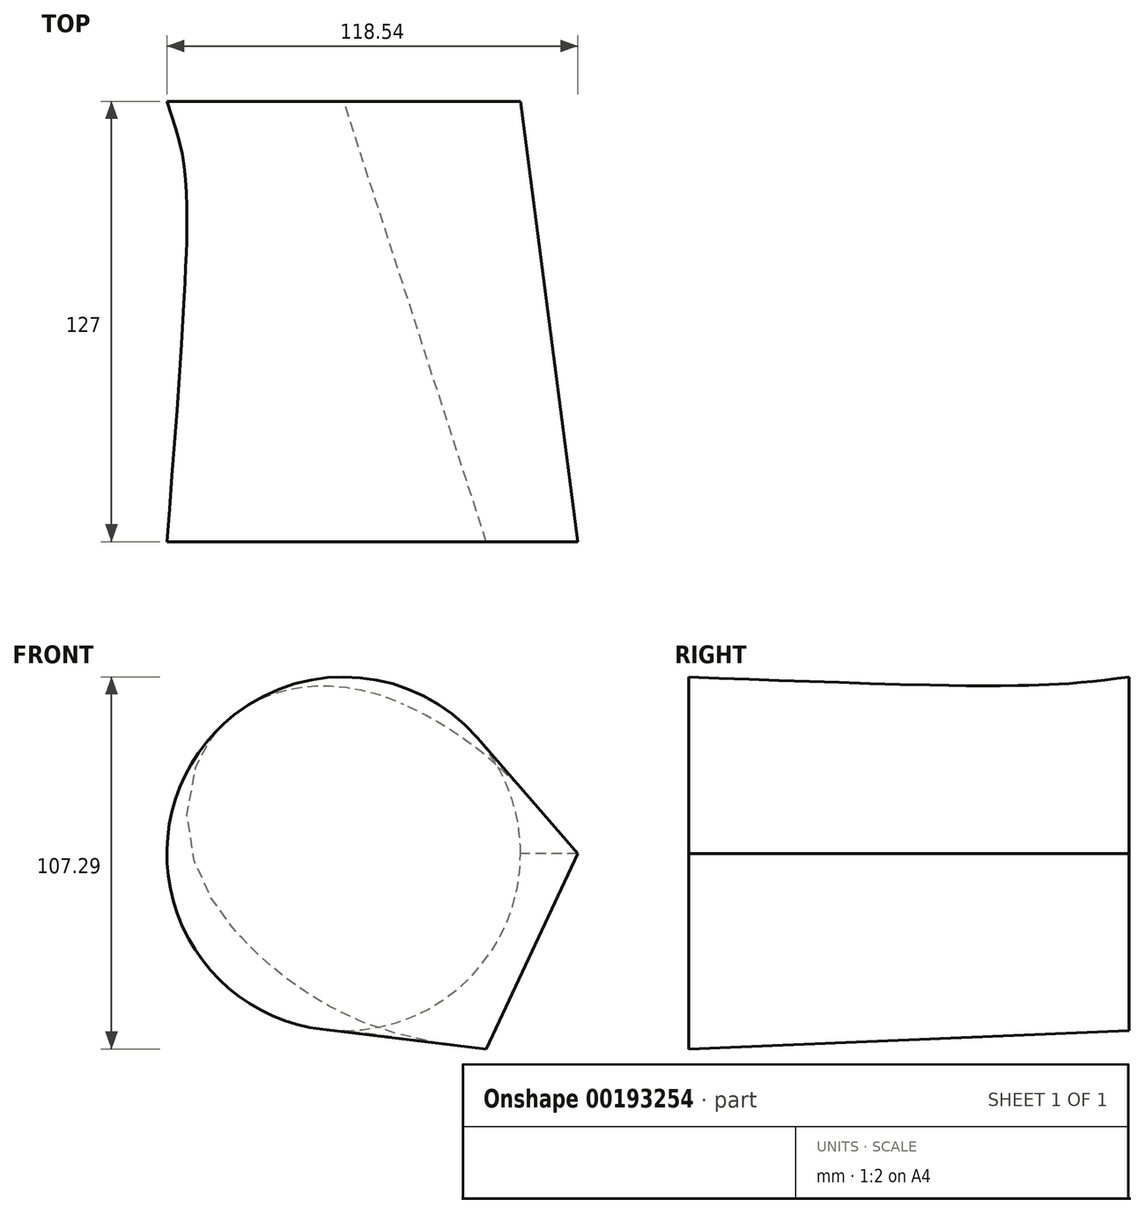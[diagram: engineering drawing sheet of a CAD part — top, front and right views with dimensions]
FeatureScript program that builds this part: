
annotation { "Feature Type Name" : "Feature", "Feature Type Description" : "" }
export const myFeature = defineFeature(function(context is Context, id is Id, definition is map)
    precondition{}
    {
        {
            var Q0;
            Q0=qCreatedBy(makeId("Front.planeOp"),FACE);
            cPlane(context, id + "F0", {"entities" : qUnion([Q0]), "cplaneType" : CPlaneType.OFFSET, "offset" : 127 * mm, "width" : 152.4 * mm, "height" : 152.4 * mm});
        }
        {
            var Q0;
            Q0=qCreatedBy(makeId("Front.planeOp"),FACE);
            var sketch = newSketch(context, id + "F1", { "sketchPlane" : qUnion([Q0])});
            skCircle(sketch, "E0", {"center": v(0, 0) * mm, "radius": 51 * mm});
            skPoint(sketch, "E1", {"position": v(51, 0) * mm});
            skSolve(sketch);
        }
        {
            var Q0;
            Q0=qCreatedBy(id+"F0.planeOp",FACE);
            var sketch = newSketch(context, id + "F2", { "sketchPlane" : qUnion([Q0])});
            skArc(sketch, "E2.0", {"start": v(38.53, 33.43) * mm, "mid": v(-45.07, 23.9) * mm, "end": v(-6.04, -50.65) * mm});
            skLineSegment(sketch, "E3", {"start": v(38.53, 33.43) * mm, "end": v(67.53, 0) * mm});
            skLineSegment(sketch, "E4", {"start": v(67.53, 0) * mm, "end": v(41.12, -56.28) * mm});
            skLineSegment(sketch, "E5", {"start": v(41.12, -56.28) * mm, "end": v(-6.04, -50.65) * mm});
            skSolve(sketch);
        }
        {
            var Q0;
            Q0=makeQuery(id+"F2.imprint","IMPRINT",FACE,{"disambiguationData":[TD([[makeQuery(id+"F2.imprint","IMPRINT",EDGE,{"derivedFrom":sQuery(id+"F2.wireOp",EDGE,"E2.0")}),1.0]])]});
            var Q1;
            Q1=makeQuery(id+"F1.imprint","IMPRINT",FACE,{"disambiguationData":[TD([[makeQuery(id+"F1.imprint","IMPRINT",EDGE,{"derivedFrom":sQuery(id+"F1.wireOp",EDGE,"E0")}),1.0]])]});
            var Q2;
            Q2=sQuery(id+"F2.wireOp",VERTEX,"E4.start");
            var Q3;
            Q3=sQuery(id+"F1.wireOp",VERTEX,"E1");
            loft(context, id + "F3", {"sheetProfilesArray" : [{ "sheetProfileEntities" : qUnion([Q0]) }, { "sheetProfileEntities" : qUnion([Q1]) }], "matchConnections" : true, "connections" : [{ "connectionEntities" : qUnion([Q2, Q3]), "connectionEdgeQueries" : qUnion([]), "connectionEdgeParameters" : [] }]});
        }
    });
